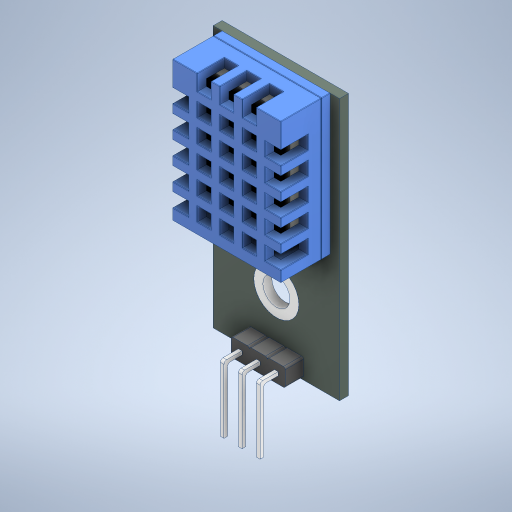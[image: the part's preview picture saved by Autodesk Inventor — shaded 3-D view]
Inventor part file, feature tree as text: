
AUTODESK INVENTOR PART (.ipt)
format: ipt  version: 2023 (Build 270158000, 158)  size: 569,856 bytes
history: imported  units: in
note: dims shown in document units (in); Inventor stores cm internally (conversion verified against a paired STEP export)
features: plane x1, imported_body x1
ambient origin geometry x8: Origin, YZ Plane, XZ Plane, XY Plane, X Axis, Y Axis, Z Axis, Center Point
bodies: Solid1 (imported_parasolid), Solid2 (imported_parasolid), Body1 (imported_parasolid), Body2 (imported_parasolid)
feature tree (2):
  plane  "Work Plane1"
  imported_body  NMx_Import_Brep_tag  [imported B-rep: ~407 faces, bbox_mm=[14.0, 35.049393, 6.5]]
